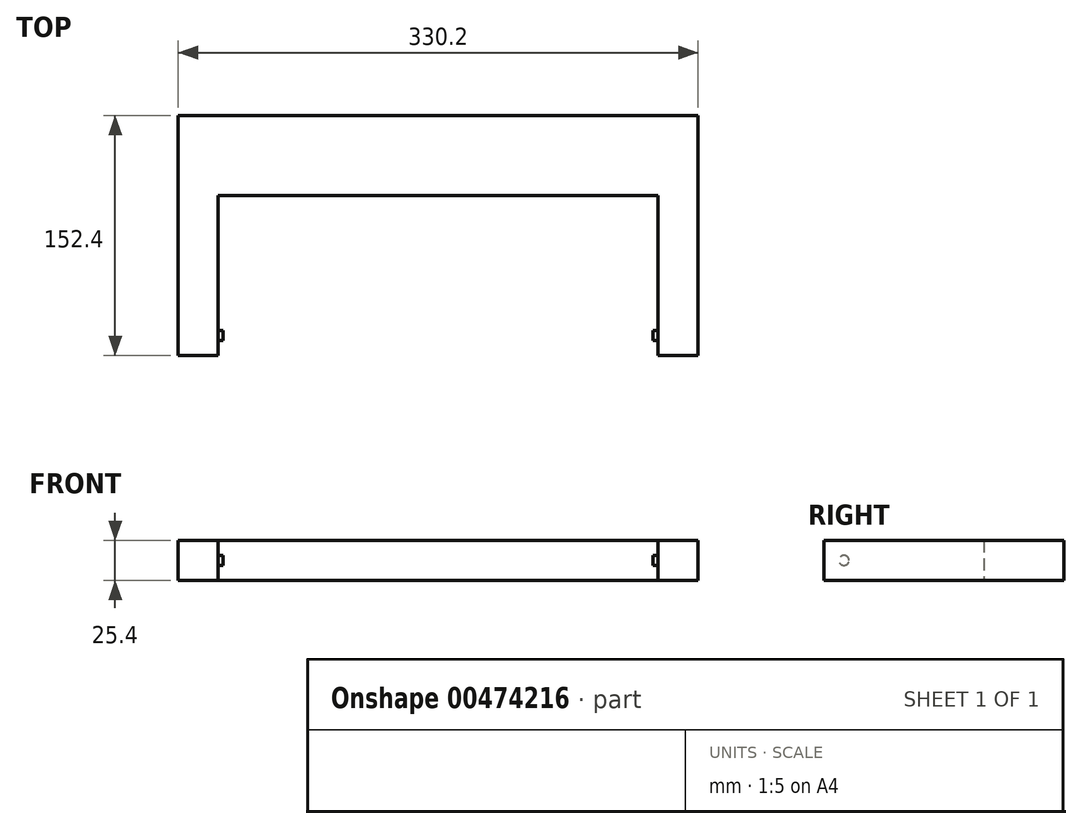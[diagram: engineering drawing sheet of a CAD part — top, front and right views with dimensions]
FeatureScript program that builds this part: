
annotation { "Feature Type Name" : "Feature", "Feature Type Description" : "" }
export const myFeature = defineFeature(function(context is Context, id is Id, definition is map)
    precondition{}
    {
        {
            var Q0;
            Q0=qCreatedBy(makeId("Top.planeOp"),FACE);
            var sketch = newSketch(context, id + "F0", { "sketchPlane" : qUnion([Q0])});
            skLineSegment(sketch, "E0.bottom", {"start": v(-139.7, 27.27) * mm, "end": v(139.7, 27.27) * mm});
            skLineSegment(sketch, "E0.top", {"start": v(-139.7, 78.07) * mm, "end": v(139.7, 78.07) * mm});
            skLineSegment(sketch, "E0.left", {"start": v(-139.7, 27.27) * mm, "end": v(-139.7, 78.07) * mm});
            skLineSegment(sketch, "E0.right", {"start": v(139.7, 27.27) * mm, "end": v(139.7, 78.07) * mm});
            skPoint(sketch, "E0.middle", {"position": v(0, 52.67) * mm});
            skLineSegment(sketch, "E1.bottom", {"start": v(-139.7, 78.07) * mm, "end": v(-165.1, 78.07) * mm});
            skLineSegment(sketch, "E1.top", {"start": v(-139.7, -74.33) * mm, "end": v(-165.1, -74.33) * mm});
            skLineSegment(sketch, "E1.left", {"start": v(-139.7, 78.07) * mm, "end": v(-139.7, -74.33) * mm});
            skLineSegment(sketch, "E1.right", {"start": v(-165.1, 78.07) * mm, "end": v(-165.1, -74.33) * mm});
            skLineSegment(sketch, "E2.bottom", {"start": v(139.7, 78.07) * mm, "end": v(165.1, 78.07) * mm});
            skLineSegment(sketch, "E2.top", {"start": v(139.7, -74.33) * mm, "end": v(165.1, -74.33) * mm});
            skLineSegment(sketch, "E2.left", {"start": v(139.7, 78.07) * mm, "end": v(139.7, -74.33) * mm});
            skLineSegment(sketch, "E2.right", {"start": v(165.1, 78.07) * mm, "end": v(165.1, -74.33) * mm});
            skSolve(sketch);
        }
        {
            var Q0;
            {var subQ0=sQuery(id+"F0.wireOp",EDGE,"E0.bottom");Q0=makeQuery(id+"F0.imprint","IMPRINT",FACE,{"disambiguationData":[TD([[makeQuery(id+"F0.imprint","IMPRINT",EDGE,{"derivedFrom":subQ0}),1.0]])]});}
            var Q1;
            {var subQ3=sQuery(id+"F0.wireOp",EDGE,"E1.bottom");Q1=makeQuery(id+"F0.imprint","IMPRINT",FACE,{"disambiguationData":[TD([[makeQuery(id+"F0.imprint","IMPRINT",EDGE,{"derivedFrom":subQ3}),1.0]])]});}
            var Q2;
            {var subQ3=sQuery(id+"F0.wireOp",EDGE,"E2.bottom");Q2=makeQuery(id+"F0.imprint","IMPRINT",FACE,{"disambiguationData":[TD([[makeQuery(id+"F0.imprint","IMPRINT",EDGE,{"derivedFrom":subQ3}),-1.0]])]});}
            extrude(context, id + "F1", {"entities" : qUnion([Q0, Q1, Q2]), "depth" : 25.4 * mm});
        }
        {
            var Q0;
            Q0=makeQuery(id+"F1.opExtrude","SWEPT_FACE",FACE,{"disambiguationData":[OSD([sQuery(id+"F0.wireOp",EDGE,"E1.left")])]});
            var sketch = newSketch(context, id + "F2", { "sketchPlane" : qUnion([Q0])});
            skCircle(sketch, "E3", {"center": v(-61.63, 12.7) * mm, "radius": 12.7 * mm});
            skPoint(sketch, "E3.centerSnap0", {"position": v(-74.33, 12.7) * mm});
            skCircle(sketch, "E4", {"center": v(-61.63, 12.7) * mm, "radius": 3.18 * mm});
            skSolve(sketch);
        }
        {
            var Q0;
            Q0=makeQuery(id+"F2.imprint","IMPRINT",FACE,{"disambiguationData":[TD([[makeQuery(id+"F2.imprint","IMPRINT",EDGE,{"derivedFrom":sQuery(id+"F2.wireOp",EDGE,"E4")}),1.0]])]});
            extrude(context, id + "F3", {"entities" : qUnion([Q0]), "operationType" : NewBodyOperationType.ADD, "depth" : 3.17 * mm});
        }
        {
            var Q0;
            Q0=makeQuery(id+"F1.opExtrude","SWEPT_BODY",BODY,{"disambiguationData":[OSD([sQuery(id+"F0.wireOp",EDGE,"E0.bottom"),sQuery(id+"F0.wireOp",EDGE,"E0.top"),sQuery(id+"F0.wireOp",EDGE,"E1.bottom"),sQuery(id+"F0.wireOp",EDGE,"E1.top"),sQuery(id+"F0.wireOp",EDGE,"E1.left"),sQuery(id+"F0.wireOp",EDGE,"E1.right"),sQuery(id+"F0.wireOp",EDGE,"E2.bottom"),sQuery(id+"F0.wireOp",EDGE,"E2.top"),sQuery(id+"F0.wireOp",EDGE,"E2.left"),sQuery(id+"F0.wireOp",EDGE,"E2.right")])]});
            var Q1;
            Q1=qCreatedBy(makeId("Right.planeOp"),FACE);
            mirror(context, id + "F4", {"operationType" : NewBodyOperationType.ADD, "entities" : qUnion([Q0]), "mirrorPlane" : qUnion([Q1])});
        }
    });
